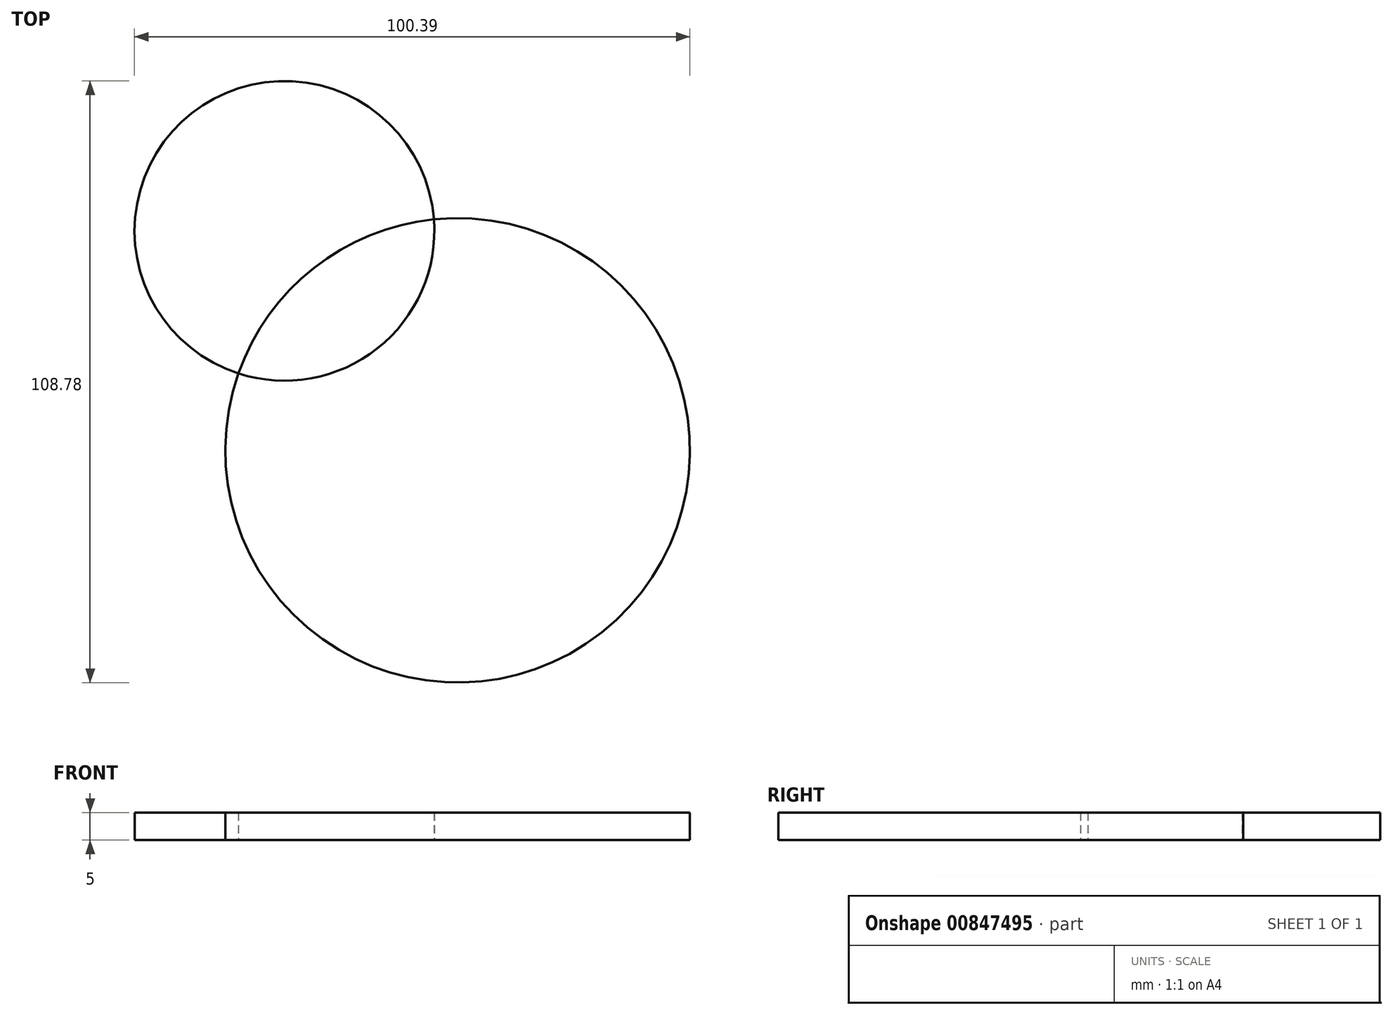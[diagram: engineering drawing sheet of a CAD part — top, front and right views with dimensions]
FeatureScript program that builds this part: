
annotation { "Feature Type Name" : "Feature", "Feature Type Description" : "" }
export const myFeature = defineFeature(function(context is Context, id is Id, definition is map)
    precondition{}
    {
        {
            var Q0;
            Q0=qCreatedBy(makeId("Top.planeOp"),FACE);
            var sketch = newSketch(context, id + "F0", { "sketchPlane" : qUnion([Q0])});
            skCircle(sketch, "E0", {"center": v(-10.58, 25.96) * mm, "radius": 27.1 * mm});
            skPoint(sketch, "E0.first.point", {"position": v(-35.1, 37.48) * mm});
            skPoint(sketch, "E0.second.point", {"position": v(16.43, 28.04) * mm});
            skPoint(sketch, "E0.third.point", {"position": v(-8.3, 52.95) * mm});
            skCircle(sketch, "E1", {"center": v(20.72, -13.73) * mm, "radius": 42 * mm});
            skPoint(sketch, "E1.second.point", {"position": v(25, 28.04) * mm});
            skPoint(sketch, "E1.third.point", {"position": v(0, -50.26) * mm});
            skSolve(sketch);
        }
        {
            var Q0;
            {var subQ0=sQuery(id+"F0.wireOp",EDGE,"E1");var subQ1=sQuery(id+"F0.wireOp",EDGE,"E0");var subQ2=makeQuery(id+"F0.imprint","INTERSECT",VERTEX,{"disambiguationData":[OD(0.0)],"derivedFrom":[subQ1,subQ0]});Q0=makeQuery(id+"F0.imprint","IMPRINT",FACE,{"disambiguationData":[TD([[makeQuery(id+"F0.imprint","IMPRINT",EDGE,{"disambiguationData":[TD([[subQ2,-1.0]])],"derivedFrom":subQ1}),-1.0]])]});}
            var Q1;
            {var subQ0=sQuery(id+"F0.wireOp",EDGE,"E1");var subQ1=sQuery(id+"F0.wireOp",EDGE,"E0");var subQ2=makeQuery(id+"F0.imprint","INTERSECT",VERTEX,{"disambiguationData":[OD(0.0)],"derivedFrom":[subQ1,subQ0]});Q1=makeQuery(id+"F0.imprint","IMPRINT",FACE,{"disambiguationData":[TD([[makeQuery(id+"F0.imprint","IMPRINT",EDGE,{"disambiguationData":[TD([[subQ2,1.0]])],"derivedFrom":subQ1}),1.0]])]});}
            extrude(context, id + "F1", {"entities" : qUnion([Q0, Q1]), "depth" : 5 * mm, "offsetDistance" : 25.4 * mm});
        }
    });
